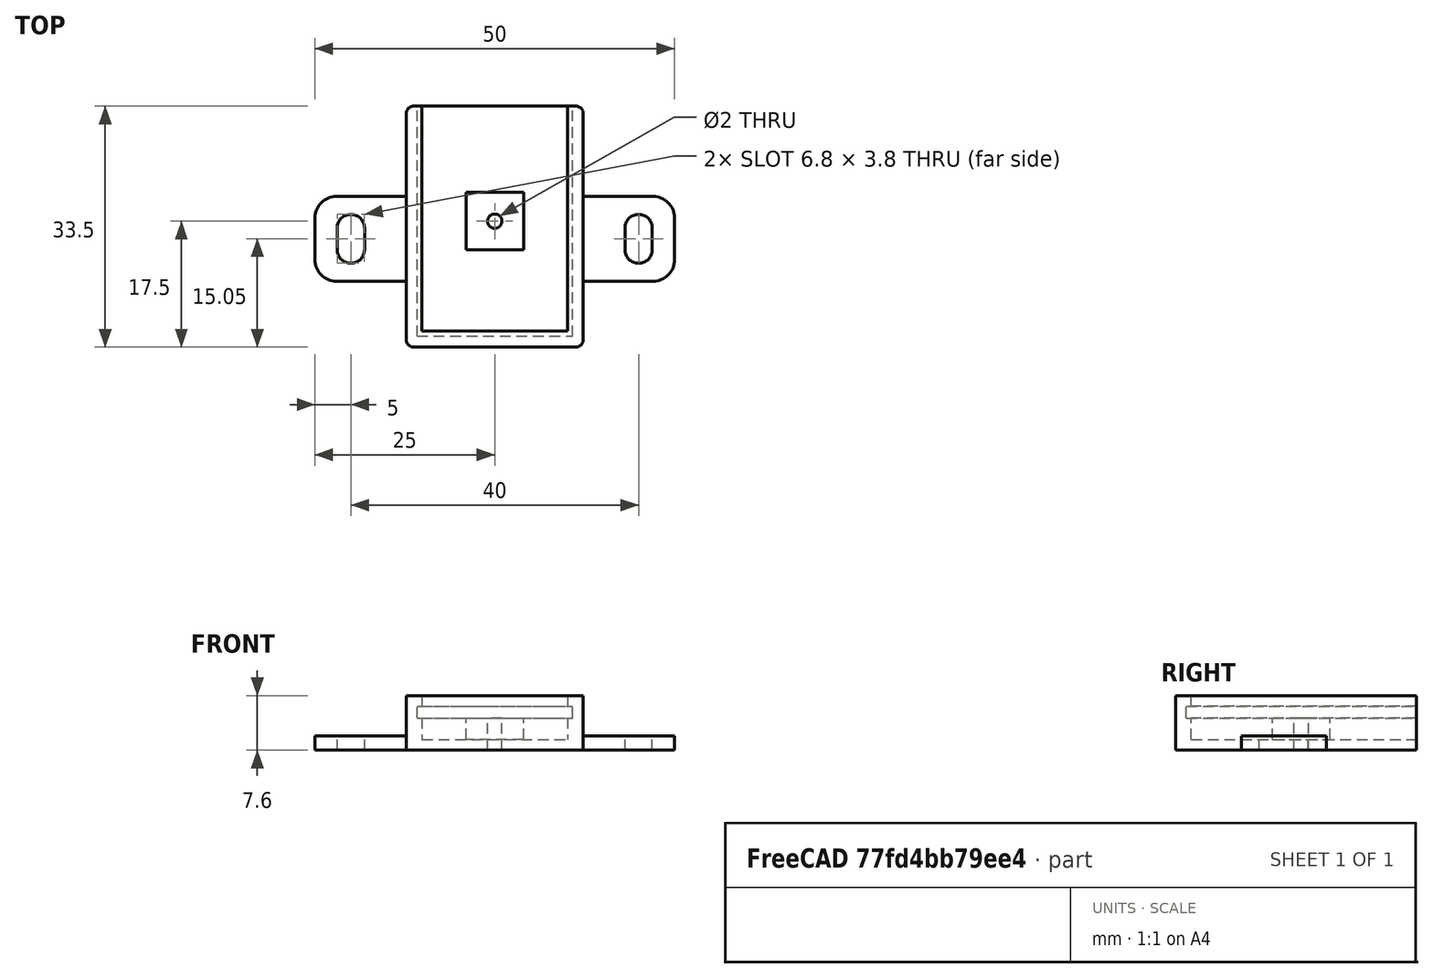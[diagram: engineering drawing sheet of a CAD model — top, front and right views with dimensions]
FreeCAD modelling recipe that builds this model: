
FCSTD DOCUMENT  (FreeCAD 0.19R23578 (Git))
Label: motor-driver-l9110s
License: FreeArt
LicenseURL: http://artlibre.org/licence/lal
objects: Part::Box×4, Part::MultiFuse×3, Part::Cut×2, Spreadsheet::Sheet×1, Part::Fillet×1, Part::Cylinder×1, Part::Feature×1, App::Part×1
note: 12 computed .brp shape members not serialized (recipe doc carries the construction recipe); baked Part::Feature solids carry a one-line shape summary decoded from their .brp

FEATURE [Spreadsheet::Sheet] Spreadsheet  label="p"
  cells = A1=pcb_x; B1(pcb_x)=21.6; A2=pcb_y; B2(pcb_y)=32; A3=pcb_z; B3(pcb_z)=1.6; A4=pcb_under; B4(pcb_under)=3; A5=side_wall; B5(side_wall)=1.5; A6=pcb_side_lane; B6(pcb_side_lane)=0.7; A7=bottom_wall; B7(bottom_wall)=1.5; A8=pcb_above; B8(pcb_above)=1.5; A9=hole_dist_x; B9(hole_dist_x)=12; A10=hole_r; B10(hole_r)=1; A11=hole_off_y; B11(hole_off_y)=16; A12=hole_stand_size; B12(hole_stand_size)=8
FEATURE [Part::Box] Box  label="external cube"
  AttacherType = Attacher::AttachEngine3D
  Height = 7.6
  Length = 24.6
  Width = 33.5
  expr: Length = <<p>>.pcb_x + 2 * <<p>>.side_wall
  expr: Width = <<p>>.pcb_y + <<p>>.side_wall
  expr: Height = <<p>>.bottom_wall + <<p>>.pcb_under + <<p>>.pcb_z + <<p>>.pcb_above
FEATURE [Part::Box] Box006  label="internal cube"
  AttacherType = Attacher::AttachEngine3D
  Height = 6.1
  Length = 20.2
  Placement = pos=(2.2,2.2,1.5) rot=(0,0,1;0rad)
  Width = 32.1
  expr: Length = <<p>>.pcb_x - 2 * <<p>>.pcb_side_lane
  expr: Width = <<p>>.pcb_y - 2 * <<p>>.pcb_side_lane + <<p>>.side_wall
  expr: Height = <<p>>.pcb_under + <<p>>.pcb_z + <<p>>.pcb_above
  expr: .Placement.Base.z = <<p>>.bottom_wall
  expr: .Placement.Base.x = <<p>>.side_wall + <<p>>.pcb_side_lane
  expr: .Placement.Base.y = <<p>>.side_wall + <<p>>.pcb_side_lane
FEATURE [Part::Box] Box007  label="pcb extract cube"
  AttacherType = Attacher::AttachEngine3D
  Height = 1.6
  Length = 21.6
  Placement = pos=(1.5,1.5,4.5) rot=(0,0,1;0rad)
  Width = 32
  expr: Height = <<p>>.pcb_z
  expr: .Placement.Base.z = <<p>>.bottom_wall + <<p>>.pcb_under
  expr: Width = <<p>>.pcb_y
  expr: Length = <<p>>.pcb_x
  expr: .Placement.Base.x = <<p>>.side_wall
  expr: .Placement.Base.y = <<p>>.side_wall
FEATURE [Part::MultiFuse] Fusion  label="extract fusion"
  Shapes = -> [Box006,Box007]
FEATURE [Part::Fillet] Fillet  label="external fillet"
  Base = -> Box
  Edges = 4 edges r=1: [Edge1,Edge3,Edge5,Edge7]
FEATURE [Part::Cylinder] Cylinder  label="hole"
  Angle = 360
  AttacherType = Attacher::AttachEngine3D
  Height = 10
  Placement = pos=(12.3,17.5,0) rot=(0,0,1;0rad)
  Radius = 1
  expr: Radius = <<p>>.hole_r
  expr: .Placement.Base.x = (2 * <<p>>.side_wall + <<p>>.pcb_x) / 2
  expr: .Placement.Base.y = <<p>>.hole_off_y + <<p>>.side_wall
FEATURE [Part::Box] Box008  label="stand"
  AttacherType = Attacher::AttachEngine3D
  Height = 4.5
  Length = 8
  Placement = pos=(8.3,13.5,0) rot=(0,0,1;0rad)
  Width = 8
  expr: .Placement.Base.y = <<p>>.hole_off_y - <<p>>.hole_stand_size / 2 + <<p>>.side_wall
  expr: .Placement.Base.x = (2 * <<p>>.side_wall + <<p>>.pcb_x) / 2 - <<p>>.hole_stand_size / 2
  expr: Width = <<p>>.hole_stand_size
  expr: Length = <<p>>.hole_stand_size
  expr: Height = <<p>>.pcb_under + <<p>>.bottom_wall
FEATURE [Part::Feature] Cut003001  label="attach plane x dir001"
  Placement = pos=(-12.7,9.15,0) rot=(0,0,1;0rad)
  shape: bbox 50 x 11.8 x 2 mm, 18 faces (baked)
FEATURE [Part::MultiFuse] Fusion001  label="body fusion"
  Shapes = -> [Fillet,Cut003001]
FEATURE [Part::Cut] Cut  label="body cut"
  Base = -> Fusion001
  Tool = -> Fusion
FEATURE [Part::MultiFuse] Fusion002  label="l9110s fusion"
  Shapes = -> [Cut,Box008]
FEATURE [Part::Cut] Cut003002  label="l9110s cut"
  Base = -> Fusion002
  Tool = -> Cylinder
FEATURE [App::Part] Part  label="l9110s pcb box part"
  Group = -> [Box,Fillet,Fusion001,Fusion,Box007,Box006,Cut,Cylinder,Box008,Fusion002,Cut003002]
  Origin = -> Origin
